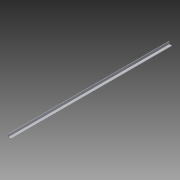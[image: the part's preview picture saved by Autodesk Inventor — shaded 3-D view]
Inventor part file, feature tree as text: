
AUTODESK INVENTOR PART (.ipt)
format: ipt  version: 2013 (Build 170138000, 138)  size: 73,216 bytes
history: native  units: in
note: dims shown in document units (in); Inventor stores cm internally (conversion verified against a paired STEP export)
features: extrude x1, sketch x1
ambient origin geometry x8: Origin, YZ Plane, XZ Plane, XY Plane, X Axis, Y Axis, Z Axis, Center Point
bodies: Solid1 (feature_tree)
feature tree (2):
  extrude  "Extrusion1"  Depth=0.0625in
  sketch  "Sketch1"  dims[d0=0.5in d1=0.0625in d2=0.5in d3=0.0625in d4=27.875in d5=0.0in]
